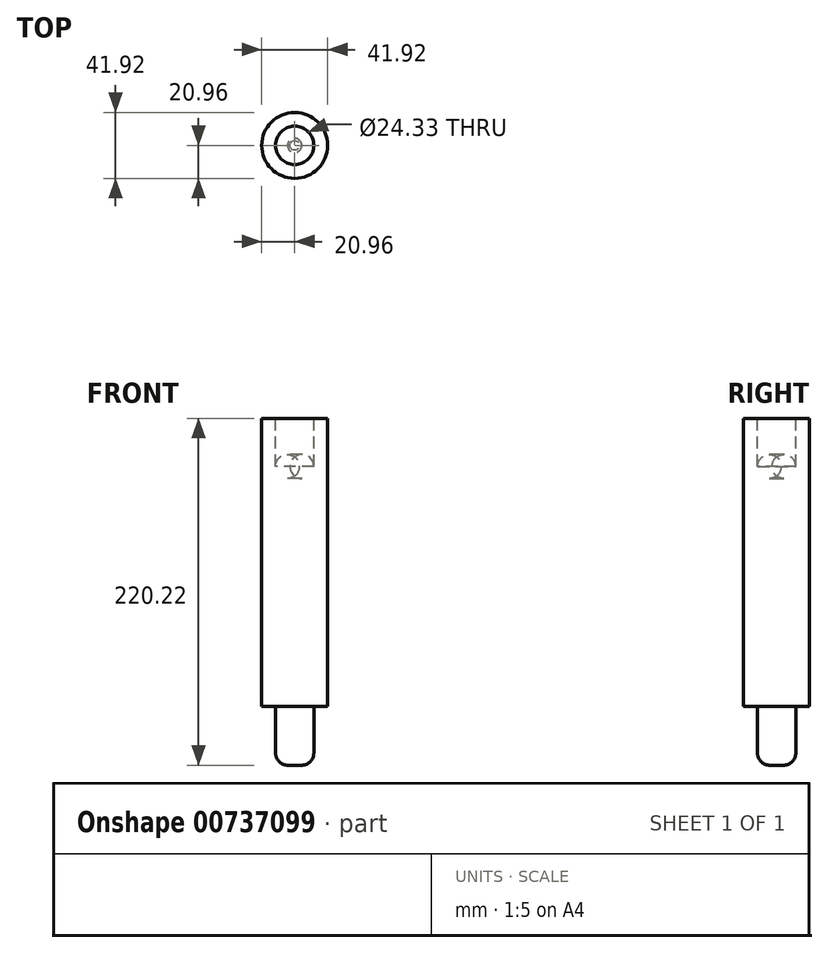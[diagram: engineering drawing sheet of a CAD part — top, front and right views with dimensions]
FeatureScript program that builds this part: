
annotation { "Feature Type Name" : "Feature", "Feature Type Description" : "" }
export const myFeature = defineFeature(function(context is Context, id is Id, definition is map)
    precondition{}
    {
        {
            var Q0;
            Q0=qCreatedBy(makeId("Top.planeOp"),FACE);
            var sketch = newSketch(context, id + "F0", { "sketchPlane" : qUnion([Q0])});
            skCircle(sketch, "E0", {"center": v(0, 0) * mm, "radius": 20.96 * mm});
            skSolve(sketch);
        }
        {
            var Q0;
            Q0=makeQuery(id+"F0.imprint","IMPRINT",FACE,{"disambiguationData":[TD([[makeQuery(id+"F0.imprint","IMPRINT",EDGE,{"derivedFrom":sQuery(id+"F0.wireOp",EDGE,"E0")}),1.0]])]});
            extrude(context, id + "F1", {"entities" : qUnion([Q0]), "depth" : 182.88 * mm, "offsetDistance" : 25.4 * mm});
        }
        {
            var Q0;
            Q0=makeQuery(id+"F1.opExtrude","CAP_FACE",FACE,{"disambiguationData":[OSD([sQuery(id+"F0.wireOp",EDGE,"E0")])],"isStart":true});
            var sketch = newSketch(context, id + "F2", { "sketchPlane" : qUnion([Q0])});
            skCircle(sketch, "E1", {"center": v(0, 0) * mm, "radius": 12.13 * mm});
            skSolve(sketch);
        }
        {
            var Q0;
            Q0=makeQuery(id+"F2.imprint","IMPRINT",FACE,{"disambiguationData":[TD([[makeQuery(id+"F2.imprint","IMPRINT",EDGE,{"derivedFrom":sQuery(id+"F2.wireOp",EDGE,"E1")}),1.0]])]});
            extrude(context, id + "F3", {"entities" : qUnion([Q0]), "operationType" : NewBodyOperationType.ADD, "depth" : 37.34 * mm, "offsetDistance" : 25.4 * mm});
        }
        {
            var Q0;
            Q0=makeQuery(id+"F3.opExtrude","CAP_EDGE",EDGE,{"disambiguationData":[OSD([sQuery(id+"F2.wireOp",EDGE,"E1")])],"isStart":false});
            fillet(context, id + "F4", {"entities" : qUnion([Q0]), "radius" : 7.62 * mm, "tangentPropagation" : true, "allowEdgeOverflow" : false});
        }
        {
            var Q0;
            Q0=makeQuery(id+"F1.opExtrude","CAP_FACE",FACE,{"disambiguationData":[OSD([sQuery(id+"F0.wireOp",EDGE,"E0")])],"isStart":false});
            var sketch = newSketch(context, id + "F5", { "sketchPlane" : qUnion([Q0])});
            skCircle(sketch, "E2", {"center": v(0, 0) * mm, "radius": 12.17 * mm});
            skSolve(sketch);
        }
        {
            var Q0;
            Q0=makeQuery(id+"F5.imprint","IMPRINT",FACE,{"disambiguationData":[TD([[makeQuery(id+"F5.imprint","IMPRINT",EDGE,{"derivedFrom":sQuery(id+"F5.wireOp",EDGE,"E2")}),1.0]])]});
            extrude(context, id + "F6", {"entities" : qUnion([Q0]), "operationType" : NewBodyOperationType.REMOVE, "oppositeDirection" : true, "depth" : 38.1 * mm, "offsetDistance" : 25.4 * mm});
        }
        {
            var Q0;
            Q0=makeQuery(id+"F6.boolean.opBoolean","COPY",EDGE,{"derivedFrom":makeQuery(id+"F6.opExtrude","CAP_EDGE",EDGE,{"disambiguationData":[OSD([sQuery(id+"F5.wireOp",EDGE,"E2")])],"isStart":false})});
            fillet(context, id + "F7", {"entities" : qUnion([Q0]), "radius" : 7.62 * mm, "tangentPropagation" : true, "allowEdgeOverflow" : false});
        }
    });
